# Revit family: Infire_Murall
name_source: partatom
category: Zabudowa
revit_build: Autodesk Revit 2018 (Build: 20180329_1100(x64)
units: mm (PartAtom-declared; Revit-internal decimal feet)

## family parameters
Numer OmniClass = 23.40.20.34.14
Obiekt nadrzędny = Powierzchnia
Punkt obliczania pomieszczeń = Nie
Tnij formami wycięć po wczytaniu = Nie
Tytuł OmniClass = Fireplaces
Współdzielony = Nie

## types (3) — shared parameters
Domyślna rzędna = 1219 mm
Gwarancja = 24 miesiące
Głębokość = 165 mm  [stored 0.541339 ft]
IfcExportAs = IfcSpaceHeaterType
Komentarze do typu = Biokominek
Materiał (obudowa) = INFIRE - biel
Materiał (szkło) = INFIRE - szkło
Model = MURALL
Obraz typu = Infire_Murall.JPG
Producent = INFIRE Biokominki
Szkło = Szyba hartowana 4 mm, przyciemniana
URL = http://www.infire.pl
Wysokość = 560 mm  [stored 1.83727 ft]

## per-type parameters (varying)
| type | Grubość ramki | Materiał (wkład) | Szerokość | Szerokość szyby | Wysokość szyby |
| MURALL 1000 | 75 mm | INFIRE - stal | 1000 mm  [stored 3.28084 ft] | 800 mm  [stored 2.62467 ft] | 100 mm  [stored 0.328084 ft] |
| MURALL 800 | 75 mm | INFIRE - czarny | 800 mm  [stored 2.62467 ft] | 600 mm | 100 mm  [stored 0.328084 ft] |
| MURALL 1200 | 125 mm  [stored 0.410105 ft] | INFIRE - stal | 1200 mm  [stored 3.93701 ft] | 850 mm  [stored 2.78871 ft] | 120 mm |

note: [stored X ft] marks values corroborated as IEEE doubles in the binary element streams (Revit-internal decimal feet)
